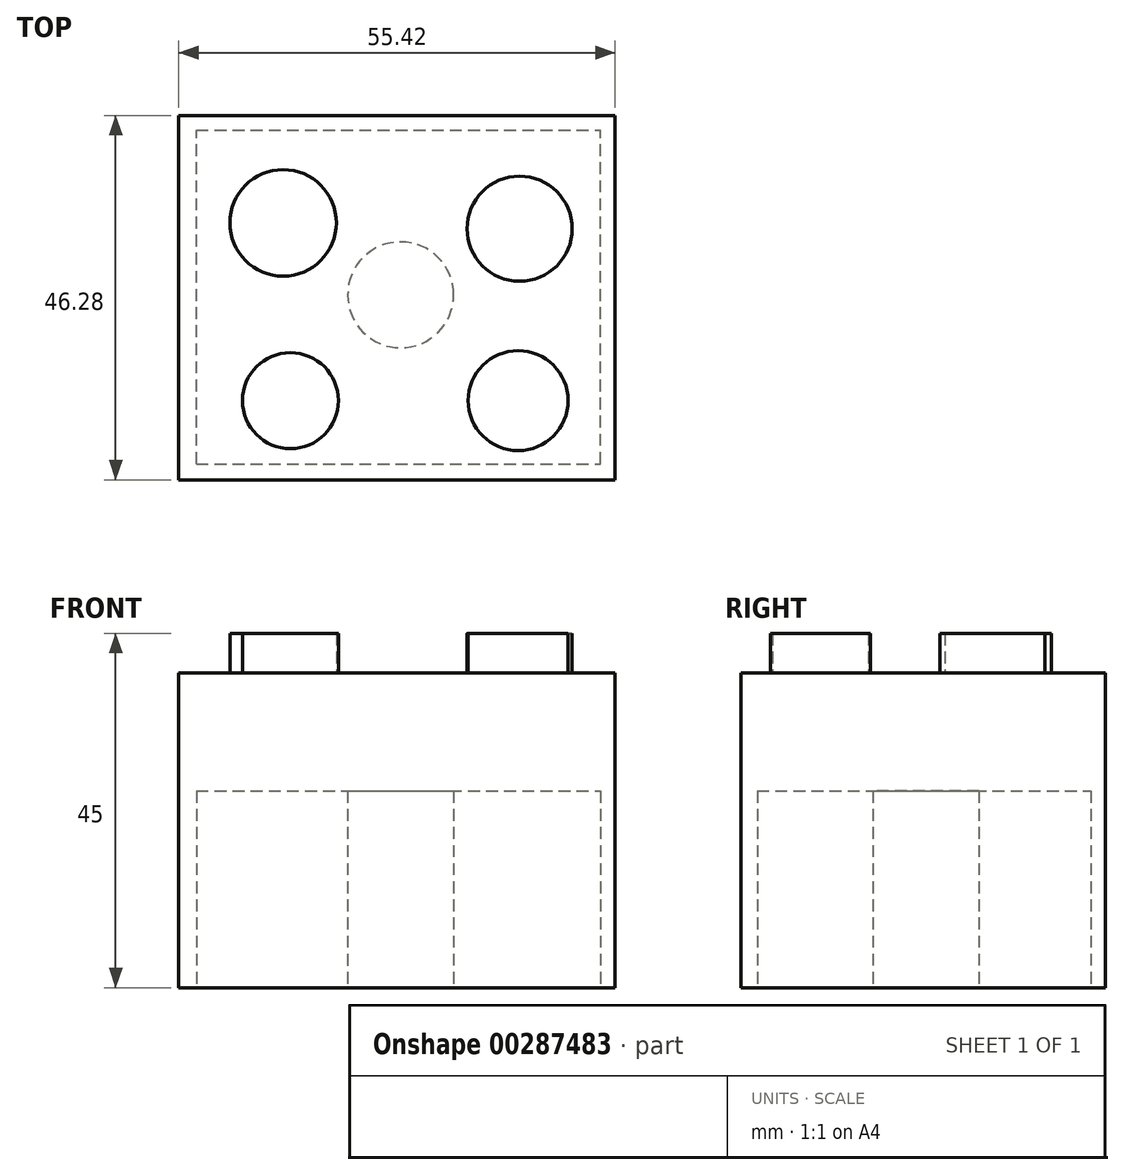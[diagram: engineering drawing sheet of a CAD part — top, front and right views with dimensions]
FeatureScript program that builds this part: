
annotation { "Feature Type Name" : "Feature", "Feature Type Description" : "" }
export const myFeature = defineFeature(function(context is Context, id is Id, definition is map)
    precondition{}
    {
        {
            var Q0;
            Q0=qCreatedBy(makeId("Top.planeOp"),FACE);
            var sketch = newSketch(context, id + "F0", { "sketchPlane" : qUnion([Q0])});
            skLineSegment(sketch, "E0.bottom", {"start": v(0, 0) * mm, "end": v(55.42, 0) * mm});
            skLineSegment(sketch, "E0.top", {"start": v(0, 46.28) * mm, "end": v(55.42, 46.28) * mm});
            skLineSegment(sketch, "E0.left", {"start": v(0, 0) * mm, "end": v(0, 46.28) * mm});
            skLineSegment(sketch, "E0.right", {"start": v(55.42, 0) * mm, "end": v(55.42, 46.28) * mm});
            skSolve(sketch);
        }
        {
            var Q0;
            Q0 = qSketchRegion(id + "F0", true);
            extrude(context, id + "F1", {"entities" : qUnion([Q0]), "depth" : 40 * mm});
        }
        {
            var Q0;
            Q0=makeQuery(id+"F1.opExtrude","CAP_FACE",FACE,{"disambiguationData":[OSD([sQuery(id+"F0.wireOp",EDGE,"E0.bottom"),sQuery(id+"F0.wireOp",EDGE,"E0.top"),sQuery(id+"F0.wireOp",EDGE,"E0.left"),sQuery(id+"F0.wireOp",EDGE,"E0.right")])],"isStart":false});
            var sketch = newSketch(context, id + "F2", { "sketchPlane" : qUnion([Q0])});
            skCircle(sketch, "E1", {"center": v(13.25, 32.66) * mm, "radius": 6.76 * mm});
            skCircle(sketch, "E2", {"center": v(43.3, 31.91) * mm, "radius": 6.67 * mm});
            skCircle(sketch, "E3", {"center": v(14.18, 10.08) * mm, "radius": 6.1 * mm});
            skCircle(sketch, "E4", {"center": v(43.1, 10.08) * mm, "radius": 6.35 * mm});
            skSolve(sketch);
        }
        {
            var Q0;
            Q0 = qSketchRegion(id + "F2", true);
            extrude(context, id + "F3", {"entities" : qUnion([Q0]), "operationType" : NewBodyOperationType.ADD, "depth" : 5 * mm});
        }
        {
            var Q0;
            Q0=makeQuery(id+"F1.opExtrude","CAP_FACE",FACE,{"disambiguationData":[OSD([sQuery(id+"F0.wireOp",EDGE,"E0.bottom"),sQuery(id+"F0.wireOp",EDGE,"E0.top"),sQuery(id+"F0.wireOp",EDGE,"E0.left"),sQuery(id+"F0.wireOp",EDGE,"E0.right")])],"isStart":true});
            var sketch = newSketch(context, id + "F4", { "sketchPlane" : qUnion([Q0])});
            skLineSegment(sketch, "E5.bottom", {"start": v(2.24, -2.05) * mm, "end": v(53.56, -2.05) * mm});
            skLineSegment(sketch, "E5.top", {"start": v(2.24, -44.41) * mm, "end": v(53.56, -44.41) * mm});
            skLineSegment(sketch, "E5.left", {"start": v(2.24, -2.05) * mm, "end": v(2.24, -44.41) * mm});
            skLineSegment(sketch, "E5.right", {"start": v(53.56, -2.05) * mm, "end": v(53.56, -44.41) * mm});
            skCircle(sketch, "E6", {"center": v(28.18, -23.51) * mm, "radius": 6.73 * mm});
            skCircle(sketch, "E7", {"center": v(28.18, -23.51) * mm, "radius": 4.9 * mm});
            skSolve(sketch);
        }
        {
            var Q0;
            Q0 = qSketchRegion(id + "F4", true);
            extrude(context, id + "F5", {"entities" : qUnion([Q0]), "operationType" : NewBodyOperationType.REMOVE, "oppositeDirection" : true, "depth" : 25 * mm});
        }
    });
